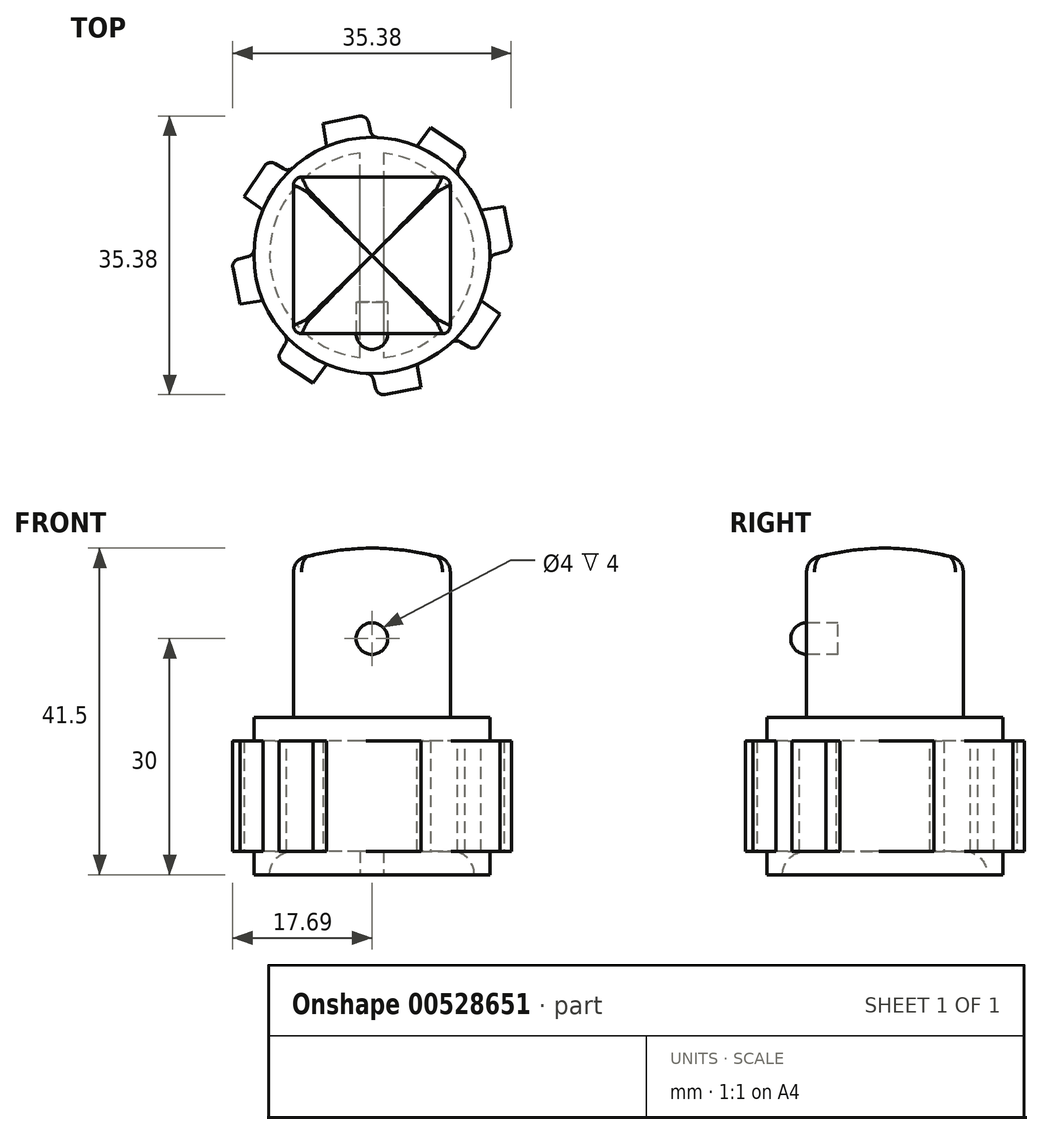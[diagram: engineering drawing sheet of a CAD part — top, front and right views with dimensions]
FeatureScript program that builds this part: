
annotation { "Feature Type Name" : "Feature", "Feature Type Description" : "" }
export const myFeature = defineFeature(function(context is Context, id is Id, definition is map)
    precondition{}
    {
        {
            var Q0;
            Q0=qCreatedBy(makeId("Top.planeOp"),FACE);
            var sketch = newSketch(context, id + "F0", { "sketchPlane" : qUnion([Q0])});
            skCircle(sketch, "E0.cCircle", {"center": v(0, 0) * mm, "radius": 9.95 * mm, "construction": true});
            skLineSegment(sketch, "E0.0", {"start": v(9.95, 9.95) * mm, "end": v(9.95, -9.95) * mm});
            skLineSegment(sketch, "E0.1", {"start": v(9.95, -9.95) * mm, "end": v(-9.95, -9.95) * mm});
            skLineSegment(sketch, "E0.2", {"start": v(-9.95, -9.95) * mm, "end": v(-9.95, 9.95) * mm});
            skLineSegment(sketch, "E0.3", {"start": v(-9.95, 9.95) * mm, "end": v(9.95, 9.95) * mm});
            skPoint(sketch, "E0.0.midPoint", {"position": v(9.95, 0) * mm});
            skSolve(sketch);
        }
        {
            var Q0;
            Q0 = qSketchRegion(id + "F0", true);
            extrude(context, id + "F1", {"entities" : qUnion([Q0]), "depth" : 20 * mm, "offsetDistance" : 25 * mm});
        }
        {
            var Q0;
            Q0=makeQuery(id+"F1.opExtrude","SWEPT_FACE",FACE,{"disambiguationData":[OSD([sQuery(id+"F0.wireOp",EDGE,"E0.1")])]});
            var sketch = newSketch(context, id + "F2", { "sketchPlane" : qUnion([Q0])});
            skArc(sketch, "E1", {"start": v(0, 8) * mm, "mid": v(2, 10) * mm, "end": v(0, 12) * mm});
            skLineSegment(sketch, "E2", {"start": v(0, 10) * mm, "end": v(0, 12) * mm});
            skLineSegment(sketch, "E3", {"start": v(0, 10) * mm, "end": v(0, 8) * mm});
            skSolve(sketch);
        }
        {
            var Q0;
            Q0=makeQuery(id+"F2.imprint","IMPRINT",FACE,{"disambiguationData":[TD([[makeQuery(id+"F2.imprint","IMPRINT",EDGE,{"derivedFrom":sQuery(id+"F2.wireOp",EDGE,"E1")}),-1.0]])]});
            var sketch = newSketch(context, id + "F3", { "sketchPlane" : qUnion([Q0])});
            skLineSegment(sketch, "E4", {"start": v(0, 12.03) * mm, "end": v(0, 8.03) * mm});
            skSolve(sketch);
        }
        {
            var Q0;
            Q0 = qSketchRegion(id + "F2", true);
            var Q1;
            Q1=sQuery(id+"F3.wireOp",EDGE,"E4");
            revolve(context, id + "F4", {"entities" : qUnion([Q0]), "axis" : qUnion([Q1]), "revolveType" : RevolveType.FULL});
        }
        {
            var Q0;
            Q0=makeQuery(id+"F1.opExtrude","SWEPT_FACE",FACE,{"disambiguationData":[OSD([sQuery(id+"F0.wireOp",EDGE,"E0.1")])]});
            var sketch = newSketch(context, id + "F5", { "sketchPlane" : qUnion([Q0])});
            skCircle(sketch, "E5", {"center": v(0, 10) * mm, "radius": 2 * mm});
            skSolve(sketch);
        }
        {
            var Q0;
            Q0 = qSketchRegion(id + "F5", true);
            extrude(context, id + "F6", {"entities" : qUnion([Q0]), "operationType" : NewBodyOperationType.REMOVE, "oppositeDirection" : true, "depth" : 4 * mm, "offsetDistance" : 25 * mm});
        }
        {
            var Q0;
            Q0=qCreatedBy(makeId("Front.planeOp"),FACE);
            var sketch = newSketch(context, id + "F7", { "sketchPlane" : qUnion([Q0])});
            skLineSegment(sketch, "E6", {"start": v(0, 20) * mm, "end": v(0, 21.5) * mm});
            skLineSegment(sketch, "E7", {"start": v(0, 20) * mm, "end": v(9.95, 20) * mm});
            skArc(sketch, "E8", {"start": v(9.95, 20) * mm, "mid": v(5.03, 21.1) * mm, "end": v(0, 21.5) * mm});
            skSolve(sketch);
        }
        {
            var Q0;
            Q0=makeQuery(id+"F7.imprint","IMPRINT",FACE,{"disambiguationData":[TD([[makeQuery(id+"F7.imprint","IMPRINT",EDGE,{"derivedFrom":sQuery(id+"F7.wireOp",EDGE,"E6")}),-1.0]])]});
            var Q1;
            Q1=makeQuery(id+"F1.opExtrude","CAP_EDGE",EDGE,{"disambiguationData":[OSD([sQuery(id+"F0.wireOp",EDGE,"E0.1")])],"isStart":false});
            var Q2;
            Q2=makeQuery(id+"F1.opExtrude","CAP_EDGE",EDGE,{"disambiguationData":[OSD([sQuery(id+"F0.wireOp",EDGE,"E0.2")])],"isStart":false});
            var Q3;
            Q3=makeQuery(id+"F1.opExtrude","CAP_EDGE",EDGE,{"disambiguationData":[OSD([sQuery(id+"F0.wireOp",EDGE,"E0.3")])],"isStart":false});
            var Q4;
            Q4=makeQuery(id+"F1.opExtrude","CAP_EDGE",EDGE,{"disambiguationData":[OSD([sQuery(id+"F0.wireOp",EDGE,"E0.0")])],"isStart":false});
            sweep(context, id + "F8", {"operationType" : NewBodyOperationType.ADD, "profiles" : qUnion([Q0]), "path" : qUnion([Q1, Q2, Q3, Q4])});
        }
        {
            var Q0;
            {var subQ0=sQuery(id+"F0.wireOp",EDGE,"E0.1");Q0=makeQuery(id+"F8.boolean.opBoolean","MERGE",EDGE,{"derivedFrom":[makeQuery(id+"F1.opExtrude","CAP_EDGE",EDGE,{"disambiguationData":[OSD([subQ0])],"isStart":false}),makeQuery(id+"F8.opSweep","SWEPT_EDGE",EDGE,{"disambiguationData":[OSD([subQ0,sQuery(id+"F7.wireOp",EDGE,"E7"),sQuery(id+"F7.wireOp",EDGE,"E8")])]})]});}
            var Q1;
            {var subQ0=sQuery(id+"F0.wireOp",EDGE,"E0.0");Q1=makeQuery(id+"F8.boolean.opBoolean","MERGE",EDGE,{"derivedFrom":[makeQuery(id+"F1.opExtrude","CAP_EDGE",EDGE,{"disambiguationData":[OSD([subQ0])],"isStart":false}),makeQuery(id+"F8.opSweep","SWEPT_EDGE",EDGE,{"disambiguationData":[OSD([subQ0,sQuery(id+"F7.wireOp",EDGE,"E7"),sQuery(id+"F7.wireOp",EDGE,"E8")])]})]});}
            var Q2;
            {var subQ0=sQuery(id+"F0.wireOp",EDGE,"E0.3");Q2=makeQuery(id+"F8.boolean.opBoolean","MERGE",EDGE,{"derivedFrom":[makeQuery(id+"F1.opExtrude","CAP_EDGE",EDGE,{"disambiguationData":[OSD([subQ0])],"isStart":false}),makeQuery(id+"F8.opSweep","SWEPT_EDGE",EDGE,{"disambiguationData":[OSD([subQ0,sQuery(id+"F7.wireOp",EDGE,"E7"),sQuery(id+"F7.wireOp",EDGE,"E8")])]})]});}
            var Q3;
            {var subQ0=sQuery(id+"F0.wireOp",EDGE,"E0.2");Q3=makeQuery(id+"F8.boolean.opBoolean","MERGE",EDGE,{"derivedFrom":[makeQuery(id+"F1.opExtrude","CAP_EDGE",EDGE,{"disambiguationData":[OSD([subQ0])],"isStart":false}),makeQuery(id+"F8.opSweep","SWEPT_EDGE",EDGE,{"disambiguationData":[OSD([subQ0,sQuery(id+"F7.wireOp",EDGE,"E7"),sQuery(id+"F7.wireOp",EDGE,"E8")])]})]});}
            fillet(context, id + "F9", {"entities" : qUnion([Q0, Q1, Q2, Q3]), "radius" : 2 * mm, "tangentPropagation" : true, "allowEdgeOverflow" : false});
        }
        {
            var Q0;
            Q0=makeQuery(id+"F1.opExtrude","SWEPT_EDGE",EDGE,{"disambiguationData":[OSD([sQuery(id+"F0.wireOp",EDGE,"E0.0"),sQuery(id+"F0.wireOp",EDGE,"E0.1")])]});
            var Q1;
            {var subQ0=sQuery(id+"F0.wireOp",EDGE,"E0.0");Q1=makeQuery(id+"F9.opFillet","BLEND_EDGE",EDGE,{"blendedFrom":[makeQuery(id+"F8.boolean.opBoolean","MERGE",EDGE,{"derivedFrom":[makeQuery(id+"F1.opExtrude","CAP_EDGE",EDGE,{"disambiguationData":[OSD([subQ0])],"isStart":false}),makeQuery(id+"F8.opSweep","SWEPT_EDGE",EDGE,{"disambiguationData":[OSD([subQ0,sQuery(id+"F7.wireOp",EDGE,"E7"),sQuery(id+"F7.wireOp",EDGE,"E8")])]})]}),makeQuery(id+"F1.opExtrude","SWEPT_FACE",FACE,{"disambiguationData":[OSD([subQ0])]})],"blendedInto":[makeQuery(id+"F1.opExtrude","SWEPT_FACE",FACE,{"disambiguationData":[OSD([subQ0])]})]});}
            var Q2;
            Q2=makeQuery(id+"F1.opExtrude","SWEPT_EDGE",EDGE,{"disambiguationData":[OSD([sQuery(id+"F0.wireOp",EDGE,"E0.0"),sQuery(id+"F0.wireOp",EDGE,"E0.3")])]});
            var Q3;
            {var subQ0=sQuery(id+"F0.wireOp",EDGE,"E0.3");Q3=makeQuery(id+"F9.opFillet","BLEND_EDGE",EDGE,{"blendedFrom":[makeQuery(id+"F8.boolean.opBoolean","MERGE",EDGE,{"derivedFrom":[makeQuery(id+"F1.opExtrude","CAP_EDGE",EDGE,{"disambiguationData":[OSD([subQ0])],"isStart":false}),makeQuery(id+"F8.opSweep","SWEPT_EDGE",EDGE,{"disambiguationData":[OSD([subQ0,sQuery(id+"F7.wireOp",EDGE,"E7"),sQuery(id+"F7.wireOp",EDGE,"E8")])]})]}),makeQuery(id+"F1.opExtrude","SWEPT_FACE",FACE,{"disambiguationData":[OSD([subQ0])]})],"blendedInto":[makeQuery(id+"F1.opExtrude","SWEPT_FACE",FACE,{"disambiguationData":[OSD([subQ0])]})]});}
            var Q4;
            Q4=makeQuery(id+"F1.opExtrude","SWEPT_EDGE",EDGE,{"disambiguationData":[OSD([sQuery(id+"F0.wireOp",EDGE,"E0.2"),sQuery(id+"F0.wireOp",EDGE,"E0.3")])]});
            var Q5;
            Q5=makeQuery(id+"F1.opExtrude","SWEPT_EDGE",EDGE,{"disambiguationData":[OSD([sQuery(id+"F0.wireOp",EDGE,"E0.1"),sQuery(id+"F0.wireOp",EDGE,"E0.2")])]});
            var Q6;
            {var subQ0=sQuery(id+"F0.wireOp",EDGE,"E0.2");Q6=makeQuery(id+"F9.opFillet","BLEND_EDGE",EDGE,{"blendedFrom":[makeQuery(id+"F8.boolean.opBoolean","MERGE",EDGE,{"derivedFrom":[makeQuery(id+"F1.opExtrude","CAP_EDGE",EDGE,{"disambiguationData":[OSD([subQ0])],"isStart":false}),makeQuery(id+"F8.opSweep","SWEPT_EDGE",EDGE,{"disambiguationData":[OSD([subQ0,sQuery(id+"F7.wireOp",EDGE,"E7"),sQuery(id+"F7.wireOp",EDGE,"E8")])]})]}),makeQuery(id+"F1.opExtrude","SWEPT_FACE",FACE,{"disambiguationData":[OSD([subQ0])]})],"blendedInto":[makeQuery(id+"F1.opExtrude","SWEPT_FACE",FACE,{"disambiguationData":[OSD([subQ0])]})]});}
            var Q7;
            {var subQ0=sQuery(id+"F0.wireOp",EDGE,"E0.1");Q7=makeQuery(id+"F9.opFillet","BLEND_EDGE",EDGE,{"blendedFrom":[makeQuery(id+"F8.boolean.opBoolean","MERGE",EDGE,{"derivedFrom":[makeQuery(id+"F1.opExtrude","CAP_EDGE",EDGE,{"disambiguationData":[OSD([subQ0])],"isStart":false}),makeQuery(id+"F8.opSweep","SWEPT_EDGE",EDGE,{"disambiguationData":[OSD([subQ0,sQuery(id+"F7.wireOp",EDGE,"E7"),sQuery(id+"F7.wireOp",EDGE,"E8")])]})]}),makeQuery(id+"F1.opExtrude","SWEPT_FACE",FACE,{"disambiguationData":[OSD([subQ0])]})],"blendedInto":[makeQuery(id+"F1.opExtrude","SWEPT_FACE",FACE,{"disambiguationData":[OSD([subQ0])]})]});}
            fillet(context, id + "F10", {"entities" : qUnion([Q0, Q1, Q2, Q3, Q4, Q5, Q6, Q7]), "radius" : 1 * mm, "tangentPropagation" : true, "allowEdgeOverflow" : false});
        }
        {
            var Q0;
            Q0=qCreatedBy(makeId("Top.planeOp"),FACE);
            var sketch = newSketch(context, id + "F11", { "sketchPlane" : qUnion([Q0])});
            skCircle(sketch, "E9", {"center": v(0, 0) * mm, "radius": 15 * mm});
            skSolve(sketch);
        }
        {
            var Q0;
            Q0=makeQuery(id+"F11.imprint","IMPRINT",FACE,{"disambiguationData":[TD([[makeQuery(id+"F11.imprint","IMPRINT",EDGE,{"derivedFrom":sQuery(id+"F11.wireOp",EDGE,"E9")}),1.0]])]});
            extrude(context, id + "F12", {"entities" : qUnion([Q0]), "operationType" : NewBodyOperationType.ADD, "oppositeDirection" : true, "depth" : 20 * mm, "offsetDistance" : 25 * mm});
        }
        {
            var Q0;
            Q0=qCreatedBy(makeId("Top.planeOp"),FACE);
            cPlane(context, id + "F13", {"entities" : qUnion([Q0]), "cplaneType" : CPlaneType.OFFSET, "offset" : 10 * mm, "oppositeDirection" : true, "width" : 150 * mm, "height" : 150 * mm});
        }
        {
            var Q0;
            Q0=qCreatedBy(id+"F13.planeOp",FACE);
            var sketch = newSketch(context, id + "F14", { "sketchPlane" : qUnion([Q0])});
            skLineSegment(sketch, "E10.1", {"start": v(-5.74, -13.86) * mm, "end": v(-10.6, -10.6) * mm});
            skLineSegment(sketch, "E10.3", {"start": v(-13.86, -5.74) * mm, "end": v(-15, 0) * mm});
            skLineSegment(sketch, "E10.5", {"start": v(-13.86, 5.74) * mm, "end": v(-10.6, 10.6) * mm});
            skLineSegment(sketch, "E10.7", {"start": v(-5.74, 13.86) * mm, "end": v(0, 15) * mm});
            skLineSegment(sketch, "E10.9", {"start": v(5.74, 13.86) * mm, "end": v(10.6, 10.6) * mm});
            skLineSegment(sketch, "E10.11", {"start": v(13.86, 5.74) * mm, "end": v(15, 0) * mm});
            skLineSegment(sketch, "E10.13", {"start": v(13.86, -5.74) * mm, "end": v(10.6, -10.6) * mm});
            skLineSegment(sketch, "E10.15", {"start": v(5.74, -13.86) * mm, "end": v(0, -15) * mm});
            skLineSegment(sketch, "E11", {"start": v(0.69, -17.86) * mm, "end": v(0, -15) * mm});
            skLineSegment(sketch, "E12", {"start": v(5.74, -13.86) * mm, "end": v(6.2, -16.77) * mm});
            skLineSegment(sketch, "E13", {"start": v(0.69, -17.86) * mm, "end": v(6.2, -16.77) * mm});
            skLineSegment(sketch, "E14", {"start": v(13.12, -12.15) * mm, "end": v(10.6, -10.6) * mm});
            skLineSegment(sketch, "E15", {"start": v(13.86, -5.74) * mm, "end": v(16.24, -7.47) * mm});
            skLineSegment(sketch, "E16", {"start": v(13.12, -12.15) * mm, "end": v(16.24, -7.47) * mm});
            skLineSegment(sketch, "E17", {"start": v(17.86, 0.69) * mm, "end": v(15, 0) * mm});
            skLineSegment(sketch, "E18", {"start": v(13.86, 5.74) * mm, "end": v(16.77, 6.2) * mm});
            skLineSegment(sketch, "E19", {"start": v(17.86, 0.69) * mm, "end": v(16.77, 6.2) * mm});
            skLineSegment(sketch, "E20", {"start": v(12.15, 13.12) * mm, "end": v(10.6, 10.6) * mm});
            skLineSegment(sketch, "E21", {"start": v(5.74, 13.86) * mm, "end": v(7.47, 16.24) * mm});
            skLineSegment(sketch, "E22", {"start": v(12.15, 13.12) * mm, "end": v(7.47, 16.24) * mm});
            skLineSegment(sketch, "E23", {"start": v(-0.69, 17.86) * mm, "end": v(0, 15) * mm});
            skLineSegment(sketch, "E24", {"start": v(-5.74, 13.86) * mm, "end": v(-6.2, 16.77) * mm});
            skLineSegment(sketch, "E25", {"start": v(-0.69, 17.86) * mm, "end": v(-6.2, 16.77) * mm});
            skLineSegment(sketch, "E26", {"start": v(-13.12, 12.15) * mm, "end": v(-10.6, 10.6) * mm});
            skLineSegment(sketch, "E27", {"start": v(-13.86, 5.74) * mm, "end": v(-16.24, 7.47) * mm});
            skLineSegment(sketch, "E28", {"start": v(-13.12, 12.15) * mm, "end": v(-16.24, 7.47) * mm});
            skLineSegment(sketch, "E29", {"start": v(-17.86, -0.69) * mm, "end": v(-15, 0) * mm});
            skLineSegment(sketch, "E30", {"start": v(-13.86, -5.74) * mm, "end": v(-16.77, -6.2) * mm});
            skLineSegment(sketch, "E31", {"start": v(-17.86, -0.69) * mm, "end": v(-16.77, -6.2) * mm});
            skLineSegment(sketch, "E32", {"start": v(-12.15, -13.12) * mm, "end": v(-10.6, -10.6) * mm});
            skLineSegment(sketch, "E33", {"start": v(-5.74, -13.86) * mm, "end": v(-7.47, -16.24) * mm});
            skLineSegment(sketch, "E34", {"start": v(-12.15, -13.12) * mm, "end": v(-7.47, -16.24) * mm});
            skSolve(sketch);
        }
        {
            var Q0;
            Q0 = qSketchRegion(id + "F14", true);
            extrude(context, id + "F15", {"entities" : qUnion([Q0]), "operationType" : NewBodyOperationType.ADD, "endBound" : BoundingType.SYMMETRIC, "depth" : 14 * mm, "offsetDistance" : 25 * mm});
        }
        {
            var Q0;
            Q0=makeQuery(id+"F15.opExtrude","SWEPT_EDGE",EDGE,{"disambiguationData":[OSD([sQuery(id+"F14.wireOp",EDGE,"E14"),sQuery(id+"F14.wireOp",EDGE,"E16")])]});
            var Q1;
            Q1=makeQuery(id+"F15.boolean.opBoolean","INTERSECT",EDGE,{"derivedFrom":[makeQuery(id+"F12.opExtrude","SWEPT_FACE",FACE,{"disambiguationData":[OSD([sQuery(id+"F11.wireOp",EDGE,"E9")])]}),makeQuery(id+"F15.opExtrude","SWEPT_FACE",FACE,{"disambiguationData":[OSD([sQuery(id+"F14.wireOp",EDGE,"E17")])]})]});
            var Q2;
            Q2=makeQuery(id+"F15.opExtrude","SWEPT_EDGE",EDGE,{"disambiguationData":[OSD([sQuery(id+"F14.wireOp",EDGE,"E17"),sQuery(id+"F14.wireOp",EDGE,"E19")])]});
            var Q3;
            Q3=makeQuery(id+"F15.boolean.opBoolean","INTERSECT",EDGE,{"derivedFrom":[makeQuery(id+"F12.opExtrude","SWEPT_FACE",FACE,{"disambiguationData":[OSD([sQuery(id+"F11.wireOp",EDGE,"E9")])]}),makeQuery(id+"F15.opExtrude","SWEPT_FACE",FACE,{"disambiguationData":[OSD([sQuery(id+"F14.wireOp",EDGE,"E20")])]})]});
            var Q4;
            Q4=makeQuery(id+"F15.opExtrude","SWEPT_EDGE",EDGE,{"disambiguationData":[OSD([sQuery(id+"F14.wireOp",EDGE,"E20"),sQuery(id+"F14.wireOp",EDGE,"E22")])]});
            var Q5;
            Q5=makeQuery(id+"F15.boolean.opBoolean","INTERSECT",EDGE,{"derivedFrom":[makeQuery(id+"F12.opExtrude","SWEPT_FACE",FACE,{"disambiguationData":[OSD([sQuery(id+"F11.wireOp",EDGE,"E9")])]}),makeQuery(id+"F15.opExtrude","SWEPT_FACE",FACE,{"disambiguationData":[OSD([sQuery(id+"F14.wireOp",EDGE,"E23")])]})]});
            var Q6;
            Q6=makeQuery(id+"F15.opExtrude","SWEPT_EDGE",EDGE,{"disambiguationData":[OSD([sQuery(id+"F14.wireOp",EDGE,"E23"),sQuery(id+"F14.wireOp",EDGE,"E25")])]});
            var Q7;
            Q7=makeQuery(id+"F15.boolean.opBoolean","INTERSECT",EDGE,{"derivedFrom":[makeQuery(id+"F12.opExtrude","SWEPT_FACE",FACE,{"disambiguationData":[OSD([sQuery(id+"F11.wireOp",EDGE,"E9")])]}),makeQuery(id+"F15.opExtrude","SWEPT_FACE",FACE,{"disambiguationData":[OSD([sQuery(id+"F14.wireOp",EDGE,"E26")])]})]});
            var Q8;
            Q8=makeQuery(id+"F15.opExtrude","SWEPT_EDGE",EDGE,{"disambiguationData":[OSD([sQuery(id+"F14.wireOp",EDGE,"E26"),sQuery(id+"F14.wireOp",EDGE,"E28")])]});
            var Q9;
            Q9=makeQuery(id+"F15.boolean.opBoolean","INTERSECT",EDGE,{"derivedFrom":[makeQuery(id+"F12.opExtrude","SWEPT_FACE",FACE,{"disambiguationData":[OSD([sQuery(id+"F11.wireOp",EDGE,"E9")])]}),makeQuery(id+"F15.opExtrude","SWEPT_FACE",FACE,{"disambiguationData":[OSD([sQuery(id+"F14.wireOp",EDGE,"E29")])]})]});
            var Q10;
            Q10=makeQuery(id+"F15.opExtrude","SWEPT_EDGE",EDGE,{"disambiguationData":[OSD([sQuery(id+"F14.wireOp",EDGE,"E29"),sQuery(id+"F14.wireOp",EDGE,"E31")])]});
            var Q11;
            Q11=makeQuery(id+"F15.boolean.opBoolean","INTERSECT",EDGE,{"derivedFrom":[makeQuery(id+"F12.opExtrude","SWEPT_FACE",FACE,{"disambiguationData":[OSD([sQuery(id+"F11.wireOp",EDGE,"E9")])]}),makeQuery(id+"F15.opExtrude","SWEPT_FACE",FACE,{"disambiguationData":[OSD([sQuery(id+"F14.wireOp",EDGE,"E32")])]})]});
            var Q12;
            Q12=makeQuery(id+"F15.opExtrude","SWEPT_EDGE",EDGE,{"disambiguationData":[OSD([sQuery(id+"F14.wireOp",EDGE,"E32"),sQuery(id+"F14.wireOp",EDGE,"E34")])]});
            var Q13;
            Q13=makeQuery(id+"F15.boolean.opBoolean","INTERSECT",EDGE,{"derivedFrom":[makeQuery(id+"F12.opExtrude","SWEPT_FACE",FACE,{"disambiguationData":[OSD([sQuery(id+"F11.wireOp",EDGE,"E9")])]}),makeQuery(id+"F15.opExtrude","SWEPT_FACE",FACE,{"disambiguationData":[OSD([sQuery(id+"F14.wireOp",EDGE,"E11")])]})]});
            var Q14;
            Q14=makeQuery(id+"F15.opExtrude","SWEPT_EDGE",EDGE,{"disambiguationData":[OSD([sQuery(id+"F14.wireOp",EDGE,"E11"),sQuery(id+"F14.wireOp",EDGE,"E13")])]});
            var Q15;
            Q15=makeQuery(id+"F15.boolean.opBoolean","INTERSECT",EDGE,{"derivedFrom":[makeQuery(id+"F12.opExtrude","SWEPT_FACE",FACE,{"disambiguationData":[OSD([sQuery(id+"F11.wireOp",EDGE,"E9")])]}),makeQuery(id+"F15.opExtrude","SWEPT_FACE",FACE,{"disambiguationData":[OSD([sQuery(id+"F14.wireOp",EDGE,"E14")])]})]});
            fillet(context, id + "F16", {"entities" : qUnion([Q0, Q1, Q2, Q3, Q4, Q5, Q6, Q7, Q8, Q9, Q10, Q11, Q12, Q13, Q14, Q15]), "radius" : 1 * mm, "tangentPropagation" : true, "allowEdgeOverflow" : false});
        }
        {
            var Q0;
            Q0=makeQuery(id+"F12.opExtrude","CAP_FACE",FACE,{"disambiguationData":[OSD([sQuery(id+"F11.wireOp",EDGE,"E9")])],"isStart":false});
            var sketch = newSketch(context, id + "F17", { "sketchPlane" : qUnion([Q0])});
            skLineSegment(sketch, "E35", {"start": v(1.5, 0) * mm, "end": v(1.5, 13) * mm});
            skLineSegment(sketch, "E36.MirrorCS", {"start": v(1.5, 0) * mm, "end": v(1.5, -13) * mm});
            skLineSegment(sketch, "E37.MirrorCS", {"start": v(-1.5, 0) * mm, "end": v(-1.5, -13) * mm});
            skLineSegment(sketch, "E38.MirrorCS", {"start": v(-1.5, 0) * mm, "end": v(-1.5, 13) * mm});
            skArc(sketch, "E39", {"start": v(1.5, -13) * mm, "mid": v(13, 0) * mm, "end": v(1.5, 13) * mm});
            skArc(sketch, "E40", {"start": v(-1.5, 13) * mm, "mid": v(-13, 0) * mm, "end": v(-1.5, -13) * mm});
            skSolve(sketch);
        }
        {
            var Q0;
            Q0 = qSketchRegion(id + "F17", true);
            extrude(context, id + "F18", {"entities" : qUnion([Q0]), "operationType" : NewBodyOperationType.REMOVE, "oppositeDirection" : true, "depth" : 3 * mm, "offsetDistance" : 25 * mm});
        }
        {
            var Q0;
            Q0=makeQuery(id+"F18.boolean.opBoolean","COPY",EDGE,{"derivedFrom":makeQuery(id+"F18.opExtrude","CAP_EDGE",EDGE,{"disambiguationData":[OSD([sQuery(id+"F17.wireOp",EDGE,"E40")])],"isStart":false})});
            var Q1;
            Q1=makeQuery(id+"F18.boolean.opBoolean","COPY",EDGE,{"derivedFrom":makeQuery(id+"F18.opExtrude","CAP_EDGE",EDGE,{"disambiguationData":[OSD([sQuery(id+"F17.wireOp",EDGE,"E39")])],"isStart":false})});
            fillet(context, id + "F19", {"entities" : qUnion([Q0, Q1]), "radius" : 3 * mm, "tangentPropagation" : true, "allowEdgeOverflow" : false});
        }
    });
